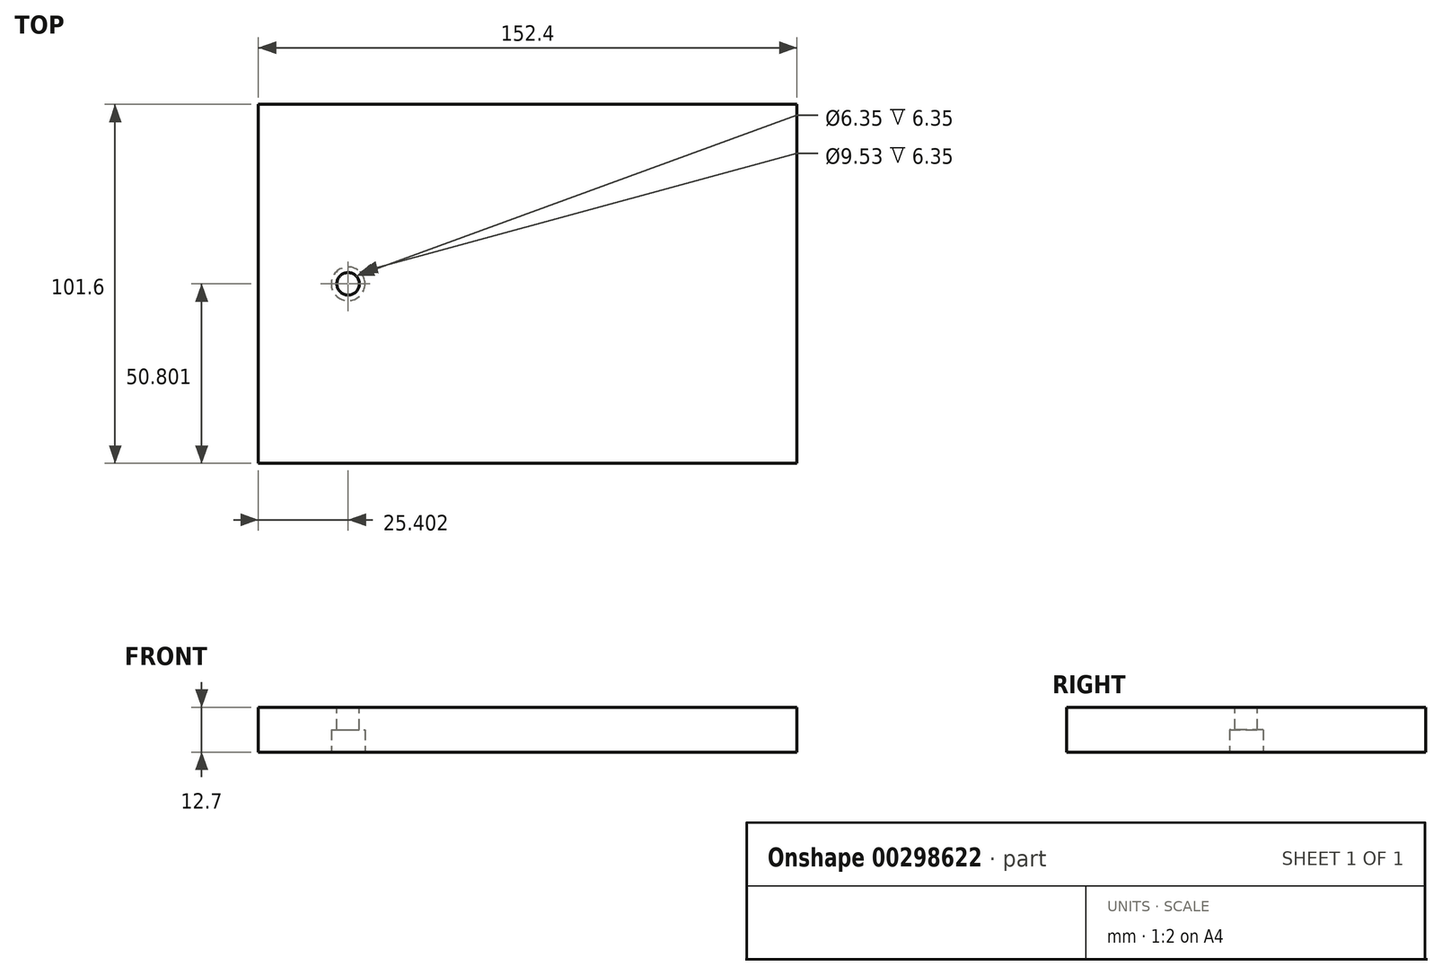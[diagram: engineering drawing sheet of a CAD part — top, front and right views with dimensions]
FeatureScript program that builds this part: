
annotation { "Feature Type Name" : "Feature", "Feature Type Description" : "" }
export const myFeature = defineFeature(function(context is Context, id is Id, definition is map)
    precondition{}
    {
        {
            var Q0;
            Q0=qCreatedBy(makeId("Top.planeOp"),FACE);
            var sketch = newSketch(context, id + "F0", { "sketchPlane" : qUnion([Q0])});
            skLineSegment(sketch, "E0.bottom", {"start": v(-74.24, 45.23) * mm, "end": v(78.16, 45.23) * mm});
            skLineSegment(sketch, "E0.top", {"start": v(-74.24, -56.37) * mm, "end": v(78.16, -56.37) * mm});
            skLineSegment(sketch, "E0.left", {"start": v(-74.24, 45.23) * mm, "end": v(-74.24, -56.37) * mm});
            skLineSegment(sketch, "E0.right", {"start": v(78.16, 45.23) * mm, "end": v(78.16, -56.37) * mm});
            skSolve(sketch);
        }
        {
            var Q0;
            Q0=makeQuery(id+"F0.imprint","IMPRINT",FACE,{"disambiguationData":[TD([[makeQuery(id+"F0.imprint","IMPRINT",EDGE,{"derivedFrom":sQuery(id+"F0.wireOp",EDGE,"E0.bottom")}),-1.0]])]});
            extrude(context, id + "F1", {"entities" : qUnion([Q0]), "depth" : 12.7 * mm});
        }
        {
            var Q0;
            Q0=makeQuery(id+"F1.opExtrude","CAP_FACE",FACE,{"disambiguationData":[OSD([sQuery(id+"F0.wireOp",EDGE,"E0.bottom"),sQuery(id+"F0.wireOp",EDGE,"E0.top"),sQuery(id+"F0.wireOp",EDGE,"E0.left"),sQuery(id+"F0.wireOp",EDGE,"E0.right")])],"isStart":false});
            var sketch = newSketch(context, id + "F2", { "sketchPlane" : qUnion([Q0])});
            skCircle(sketch, "E1", {"center": v(-48.84, -5.57) * mm, "radius": 3.18 * mm});
            skSolve(sketch);
        }
        {
            var Q0;
            Q0 = qSketchRegion(id + "F2", true);
            var Q1;
            Q1=sQuery(id+"F2.wireOp",EDGE,"E1");
            extrude(context, id + "F3", {"entities" : qUnion([Q0]), "operationType" : NewBodyOperationType.REMOVE, "surfaceEntities" : qUnion([Q1]), "endBound" : BoundingType.THROUGH_ALL, "oppositeDirection" : true, "depth" : 25.4 * mm});
        }
        {
            var Q0;
            Q0=makeQuery(id+"F1.opExtrude","CAP_FACE",FACE,{"disambiguationData":[OSD([sQuery(id+"F0.wireOp",EDGE,"E0.bottom"),sQuery(id+"F0.wireOp",EDGE,"E0.top"),sQuery(id+"F0.wireOp",EDGE,"E0.left"),sQuery(id+"F0.wireOp",EDGE,"E0.right")])],"isStart":true});
            var sketch = newSketch(context, id + "F4", { "sketchPlane" : qUnion([Q0])});
            skCircle(sketch, "E2", {"center": v(-48.84, 5.57) * mm, "radius": 4.76 * mm});
            skSolve(sketch);
        }
        {
            var Q0;
            Q0 = qSketchRegion(id + "F4", true);
            extrude(context, id + "F5", {"entities" : qUnion([Q0]), "operationType" : NewBodyOperationType.REMOVE, "oppositeDirection" : true, "depth" : 6.35 * mm});
        }
    });
